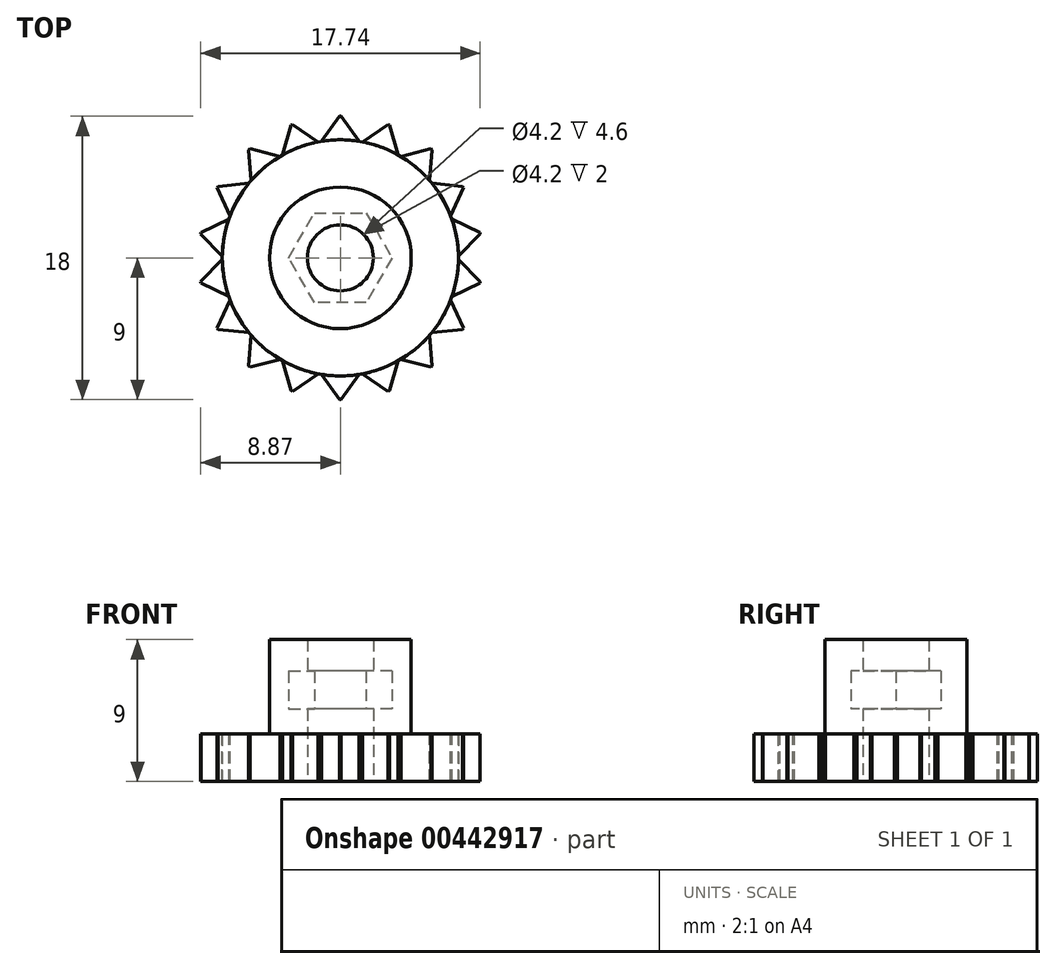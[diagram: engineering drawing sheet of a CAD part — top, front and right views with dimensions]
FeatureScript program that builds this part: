
annotation { "Feature Type Name" : "Feature", "Feature Type Description" : "" }
export const myFeature = defineFeature(function(context is Context, id is Id, definition is map)
    precondition{}
    {
        {
            var Q0;
            Q0=qCreatedBy(makeId("Top.planeOp"),FACE);
            var sketch = newSketch(context, id + "F0", { "sketchPlane" : qUnion([Q0])});
            skCircle(sketch, "E0", {"center": v(0, 0) * mm, "radius": 7.5 * mm});
            skCircle(sketch, "E1", {"center": v(0, 0) * mm, "radius": 4.5 * mm});
            skCircle(sketch, "E2.cCircle", {"center": v(0, 0) * mm, "radius": 2.85 * mm, "construction": true});
            skLineSegment(sketch, "E2.0", {"start": v(1.65, -2.85) * mm, "end": v(-1.65, -2.85) * mm});
            skLineSegment(sketch, "E2.1", {"start": v(-1.65, -2.85) * mm, "end": v(-3.3, 0) * mm});
            skLineSegment(sketch, "E2.2", {"start": v(-3.3, 0) * mm, "end": v(-1.65, 2.85) * mm});
            skLineSegment(sketch, "E2.3", {"start": v(-1.65, 2.85) * mm, "end": v(1.65, 2.85) * mm});
            skLineSegment(sketch, "E2.4", {"start": v(1.65, 2.85) * mm, "end": v(3.3, 0) * mm});
            skLineSegment(sketch, "E2.5", {"start": v(3.3, 0) * mm, "end": v(1.65, -2.85) * mm});
            skPoint(sketch, "E2.0.midPoint", {"position": v(0, -2.85) * mm});
            skCircle(sketch, "E3", {"center": v(0, 0) * mm, "radius": 2.1 * mm});
            skSolve(sketch);
        }
        {
            var Q0;
            Q0=makeQuery(id+"F0.imprint","IMPRINT",FACE,{"disambiguationData":[TD([[makeQuery(id+"F0.imprint","IMPRINT",EDGE,{"derivedFrom":sQuery(id+"F0.wireOp",EDGE,"E1")}),1.0]])]});
            var Q1;
            Q1=makeQuery(id+"F0.imprint","IMPRINT",FACE,{"disambiguationData":[TD([[makeQuery(id+"F0.imprint","IMPRINT",EDGE,{"derivedFrom":sQuery(id+"F0.wireOp",EDGE,"E2.0")}),-1.0]])]});
            extrude(context, id + "F1", {"entities" : qUnion([Q0, Q1]), "depth" : 9 * mm});
        }
        {
            var Q0;
            Q0=makeQuery(id+"F0.imprint","IMPRINT",FACE,{"disambiguationData":[TD([[makeQuery(id+"F0.imprint","IMPRINT",EDGE,{"derivedFrom":sQuery(id+"F0.wireOp",EDGE,"E0")}),1.0]])]});
            extrude(context, id + "F2", {"entities" : qUnion([Q0]), "operationType" : NewBodyOperationType.ADD, "depth" : 3 * mm});
        }
        {
            var Q0;
            Q0=makeQuery(id+"F0.imprint","IMPRINT",FACE,{"disambiguationData":[TD([[makeQuery(id+"F0.imprint","IMPRINT",EDGE,{"derivedFrom":sQuery(id+"F0.wireOp",EDGE,"E2.0")}),-1.0]])]});
            extrude(context, id + "F3", {"entities" : qUnion([Q0]), "operationType" : NewBodyOperationType.REMOVE, "depth" : 7 * mm, "hasSecondDirection" : true, "secondDirectionOppositeDirection" : false, "secondDirectionDepth" : 4.6 * mm});
        }
        {
            var Q0;
            Q0=makeQuery(id+"F2.opExtrude","CAP_FACE",FACE,{"disambiguationData":[OSD([sQuery(id+"F0.wireOp",EDGE,"E0"),sQuery(id+"F0.wireOp",EDGE,"E1")])],"isStart":false});
            var sketch = newSketch(context, id + "F4", { "sketchPlane" : qUnion([Q0])});
            skCircle(sketch, "E4.0", {"center": v(0, 0) * mm, "radius": 7.5 * mm});
            skLineSegment(sketch, "E5", {"start": v(-1.2, -7.4) * mm, "end": v(-0.05, -9) * mm});
            skLineSegment(sketch, "E6", {"start": v(-0.05, -9) * mm, "end": v(0.05, -9) * mm});
            skLineSegment(sketch, "E7", {"start": v(0.05, -9) * mm, "end": v(1.2, -7.4) * mm});
            skPoint(sketch, "E8", {"position": v(0, -9) * mm});
            skLineSegment(sketch, "E9", {"start": v(0, -9.03) * mm, "end": v(0, -7.2) * mm, "construction": true});
            skSolve(sketch);
        }
        {
            var Q0;
            {var subQ0=sQuery(id+"F4.wireOp",EDGE,"xMfUHdH3-sUiR-HnJx-IQe0-Awc9sF2Xy2mM");Q0=makeQuery(id+"F4.imprint","IMPRINT",FACE,{"disambiguationData":[TD([[makeQuery(id+"F4.imprint","IMPRINT",EDGE,{"derivedFrom":subQ0}),1.0]])]});}
            var Q1;
            {var subQ0=sQuery(id+"F4.wireOp",EDGE,"E5");Q1=makeQuery(id+"F4.imprint","IMPRINT",FACE,{"disambiguationData":[TD([[makeQuery(id+"F4.imprint","IMPRINT",EDGE,{"derivedFrom":subQ0}),1.0]])]});}
            var Q2;
            {var subQ0=sQuery(id+"F0.wireOp",EDGE,"E1");Q2=makeQuery(id+"F2.boolean.opBoolean","MERGE",FACE,{"derivedFrom":[makeQuery(id+"F1.opExtrude","CAP_FACE",FACE,{"disambiguationData":[OSD([subQ0,sQuery(id+"F0.wireOp",EDGE,"E3")])],"isStart":true}),makeQuery(id+"F2.opExtrude","CAP_FACE",FACE,{"disambiguationData":[OSD([sQuery(id+"F0.wireOp",EDGE,"E0"),subQ0])],"isStart":true})]});}
            extrude(context, id + "F5", {"entities" : qUnion([Q0, Q1]), "endBound" : BoundingType.UP_TO_SURFACE, "oppositeDirection" : true, "endBoundEntityFace" : qUnion([Q2]), "depth" : 25 * mm});
        }
        {
            var Q0;
            Q0=makeQuery(id+"F5.opExtrude","SWEPT_BODY",BODY,{"disambiguationData":[OSD([sQuery(id+"F4.wireOp",EDGE,"E4.0"),sQuery(id+"F4.wireOp",EDGE,"xMfUHdH3-sUiR-HnJx-IQe0-Awc9sF2Xy2mM")])]});
            var Q1;
            Q1=makeQuery(id+"F2.opExtrude","SWEPT_FACE",FACE,{"disambiguationData":[OSD([sQuery(id+"F0.wireOp",EDGE,"E0")])]});
            circularPattern(context, id + "F6", {"entities" : qUnion([Q0]), "axis" : qUnion([Q1]), "angle" : 360 * degree, "instanceCount" : 18, "equalSpace" : true});
        }
    });
